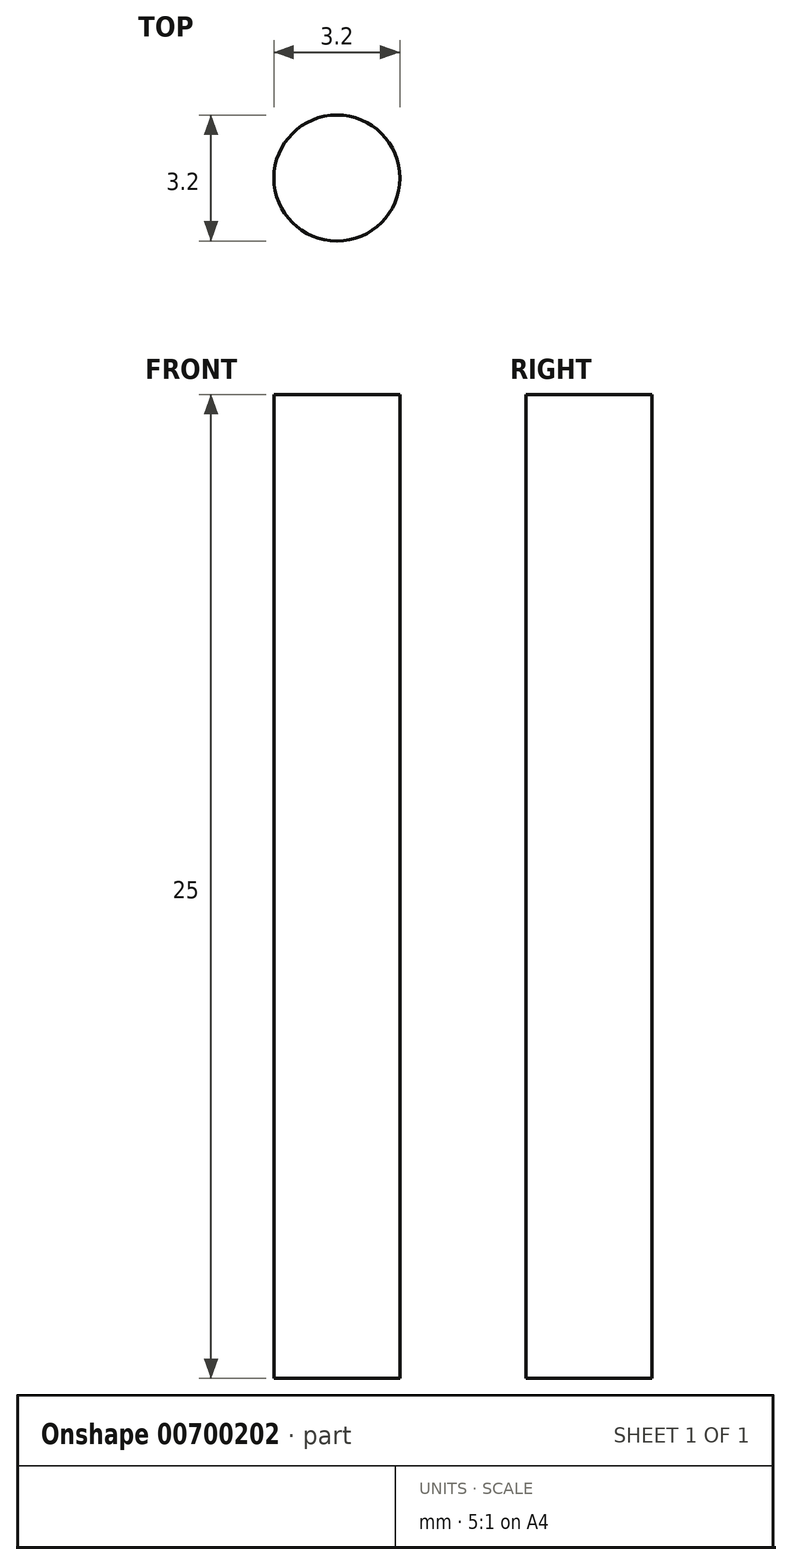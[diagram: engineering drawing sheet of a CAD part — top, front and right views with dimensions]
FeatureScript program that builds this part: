
annotation { "Feature Type Name" : "Feature", "Feature Type Description" : "" }
export const myFeature = defineFeature(function(context is Context, id is Id, definition is map)
    precondition{}
    {
        {
            var Q0;
            Q0=qCreatedBy(makeId("Top.planeOp"),FACE);
            var sketch = newSketch(context, id + "F0", { "sketchPlane" : qUnion([Q0])});
            skCircle(sketch, "E0", {"center": v(0, 0) * mm, "radius": 1.6 * mm});
            skSolve(sketch);
        }
        {
            var Q0;
            Q0=qSketchRegion(id+"F0",true);
            extrude(context, id + "F1", {"entities" : qUnion([Q0]), "depth" : 25 * mm, "offsetDistance" : 25 * mm});
        }
    });
